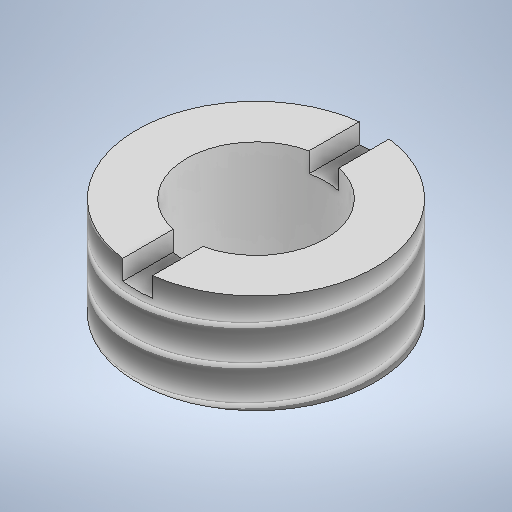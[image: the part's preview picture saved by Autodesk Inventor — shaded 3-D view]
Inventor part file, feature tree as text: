
AUTODESK INVENTOR PART (.ipt)
format: ipt  version: 2025.1 (Build 291241000, 241)  size: 278,016 bytes
history: native  units: mm
features: extrude x2, sketch x2, thread x1
ambient origin geometry x8: Origin, YZ Plane, XZ Plane, XY Plane, X Axis, Y Axis, Z Axis, Center Point
bodies: Solid1 (feature_tree)
feature tree (5):
  extrude  "Extrusion1"  Depth=5.0mm
  thread  "Thread1"  [1 undecoded]
  extrude  "Extrusion2"  Depth=1.5mm
  sketch  "Sketch1"  dims[d0=12.0mm d1=7.0mm d2=5.0mm d3=0.0mm]
  sketch  "Sketch2"  dims[d4=10.0mm d5=0.0mm d6=1.5mm d7=1.0mm d8=0.0mm]
note: 1 required parameter value undecoded (feature->parameter linkage not recoverable at this tier; creation-order binding heuristic only, values carry confidence <= 0.55)
